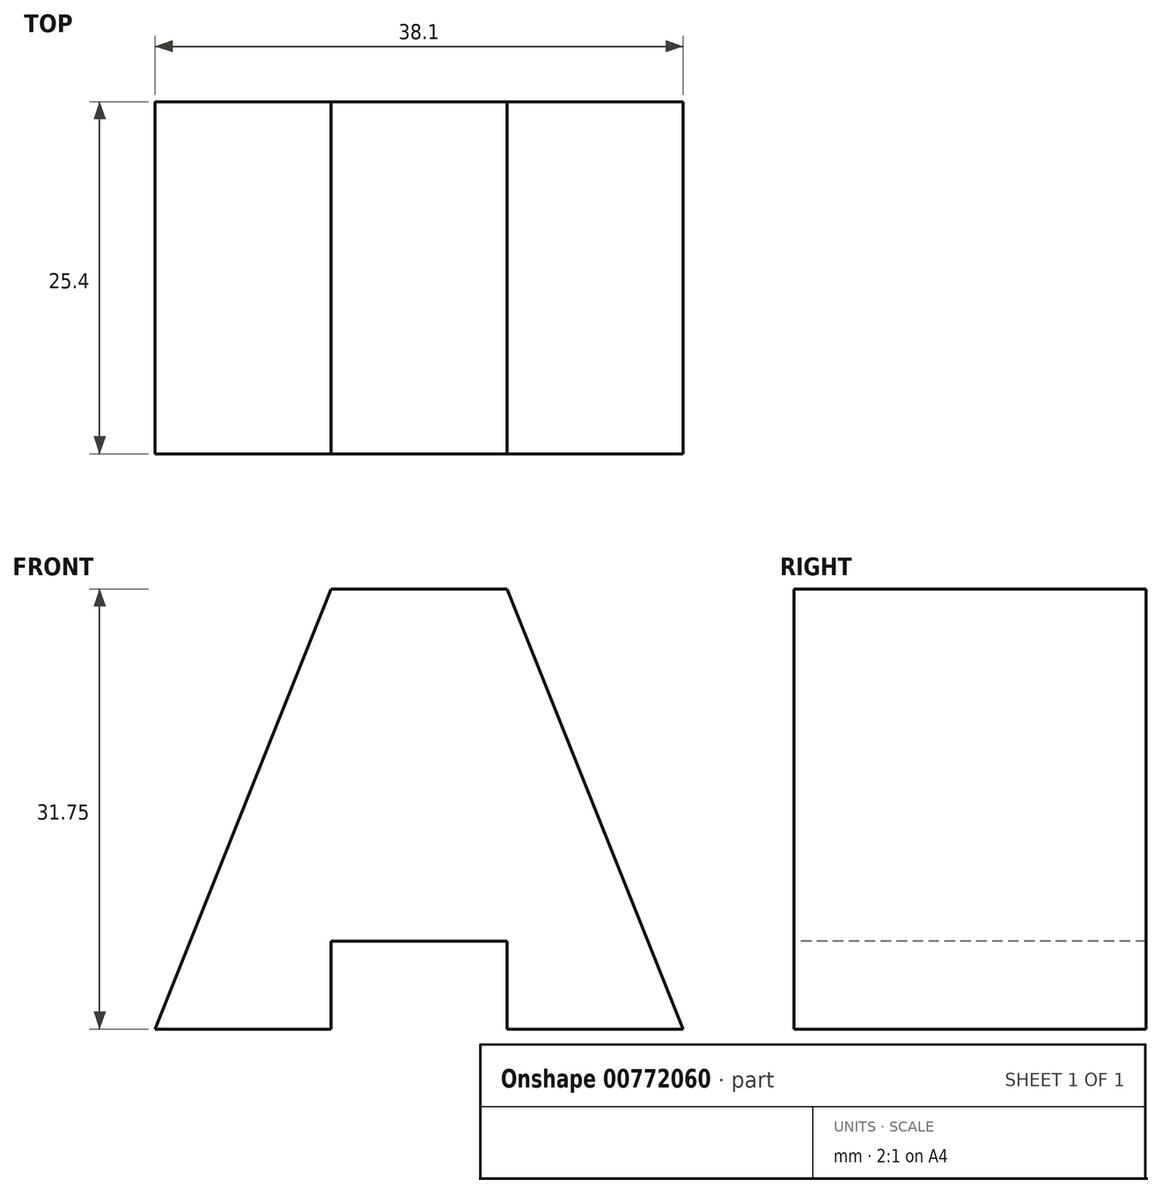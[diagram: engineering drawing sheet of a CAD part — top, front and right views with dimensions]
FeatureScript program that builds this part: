
annotation { "Feature Type Name" : "Feature", "Feature Type Description" : "" }
export const myFeature = defineFeature(function(context is Context, id is Id, definition is map)
    precondition{}
    {
        {
            var Q0;
            Q0=qCreatedBy(makeId("Front.planeOp"),FACE);
            var sketch = newSketch(context, id + "F0", { "sketchPlane" : qUnion([Q0])});
            skLineSegment(sketch, "E0", {"start": v(0, 0) * mm, "end": v(38.1, 0) * mm});
            skLineSegment(sketch, "E1", {"start": v(38.1, 0) * mm, "end": v(38.1, 31.75) * mm});
            skLineSegment(sketch, "E2", {"start": v(38.1, 31.75) * mm, "end": v(0, 31.75) * mm});
            skLineSegment(sketch, "E3", {"start": v(0, 31.75) * mm, "end": v(0, 0) * mm});
            skSolve(sketch);
        }
        {
            var Q0;
            Q0 = qSketchRegion(id + "F0", true);
            extrude(context, id + "F1", {"entities" : qUnion([Q0]), "depth" : 25.4 * mm, "offsetDistance" : 25.4 * mm});
        }
        {
            var Q0;
            Q0=makeQuery(id+"F1.opExtrude","CAP_FACE",FACE,{"disambiguationData":[OSD([sQuery(id+"F0.wireOp",EDGE,"E0"),sQuery(id+"F0.wireOp",EDGE,"E1"),sQuery(id+"F0.wireOp",EDGE,"E2"),sQuery(id+"F0.wireOp",EDGE,"E3")])],"isStart":false});
            var sketch = newSketch(context, id + "F2", { "sketchPlane" : qUnion([Q0])});
            skLineSegment(sketch, "E4", {"start": v(0, 0) * mm, "end": v(12.7, 0) * mm});
            skLineSegment(sketch, "E5", {"start": v(12.7, 0) * mm, "end": v(12.7, 6.35) * mm});
            skLineSegment(sketch, "E6", {"start": v(12.7, 6.35) * mm, "end": v(25.4, 6.35) * mm});
            skLineSegment(sketch, "E7", {"start": v(25.4, 6.35) * mm, "end": v(25.4, 0) * mm});
            skLineSegment(sketch, "E8", {"start": v(25.4, 0) * mm, "end": v(38.1, 0) * mm});
            skSolve(sketch);
        }
        {
            var Q0;
            {var subQ0=sQuery(id+"F2.wireOp",EDGE,"E5");Q0=makeQuery(id+"F2.imprint","IMPRINT",FACE,{"disambiguationData":[TD([[makeQuery(id+"F2.imprint","IMPRINT",EDGE,{"derivedFrom":subQ0}),-1.0]])]});}
            extrude(context, id + "F3", {"entities" : qUnion([Q0]), "operationType" : NewBodyOperationType.REMOVE, "oppositeDirection" : true, "depth" : 25.4 * mm, "offsetDistance" : 25.4 * mm});
        }
        {
            var Q0;
            Q0=makeQuery(id+"F1.opExtrude","CAP_FACE",FACE,{"disambiguationData":[OSD([sQuery(id+"F0.wireOp",EDGE,"E0"),sQuery(id+"F0.wireOp",EDGE,"E1"),sQuery(id+"F0.wireOp",EDGE,"E2"),sQuery(id+"F0.wireOp",EDGE,"E3")])],"isStart":false});
            var sketch = newSketch(context, id + "F4", { "sketchPlane" : qUnion([Q0])});
            skLineSegment(sketch, "E9", {"start": v(38.1, 31.75) * mm, "end": v(25.4, 31.75) * mm});
            skLineSegment(sketch, "E10", {"start": v(0, 31.75) * mm, "end": v(12.7, 31.75) * mm});
            skLineSegment(sketch, "E11", {"start": v(12.7, 31.75) * mm, "end": v(0, 0) * mm});
            skLineSegment(sketch, "E12", {"start": v(25.4, 31.75) * mm, "end": v(38.1, 0) * mm});
            skSolve(sketch);
        }
        {
            var Q0;
            Q0=makeQuery(id+"F4.imprint","IMPRINT",FACE,{"disambiguationData":[TD([[makeQuery(id+"F4.imprint","IMPRINT",EDGE,{"derivedFrom":sQuery(id+"F4.wireOp",EDGE,"E9")}),1.0]])]});
            extrude(context, id + "F5", {"entities" : qUnion([Q0]), "operationType" : NewBodyOperationType.REMOVE, "oppositeDirection" : true, "depth" : 25.4 * mm, "offsetDistance" : 25.4 * mm});
        }
        {
            var Q0;
            Q0=makeQuery(id+"F1.opExtrude","CAP_FACE",FACE,{"disambiguationData":[OSD([sQuery(id+"F0.wireOp",EDGE,"E0"),sQuery(id+"F0.wireOp",EDGE,"E1"),sQuery(id+"F0.wireOp",EDGE,"E2"),sQuery(id+"F0.wireOp",EDGE,"E3")])],"isStart":false});
            var sketch = newSketch(context, id + "F6", { "sketchPlane" : qUnion([Q0])});
            skLineSegment(sketch, "E13", {"start": v(0, 31.75) * mm, "end": v(12.7, 31.75) * mm});
            skLineSegment(sketch, "E14", {"start": v(12.7, 31.75) * mm, "end": v(0, 0) * mm});
            skSolve(sketch);
        }
        {
            var Q0;
            Q0 = qSketchRegion(id + "F6", true);
            var Q1;
            Q1=makeQuery(id+"F6.imprint","IMPRINT",FACE,{"disambiguationData":[TD([[makeQuery(id+"F6.imprint","IMPRINT",EDGE,{"derivedFrom":sQuery(id+"F6.wireOp",EDGE,"E13")}),1.0]])]});
            extrude(context, id + "F7", {"entities" : qUnion([Q0, Q1]), "operationType" : NewBodyOperationType.REMOVE, "oppositeDirection" : true, "depth" : 25.4 * mm, "offsetDistance" : 25.4 * mm});
        }
    });
